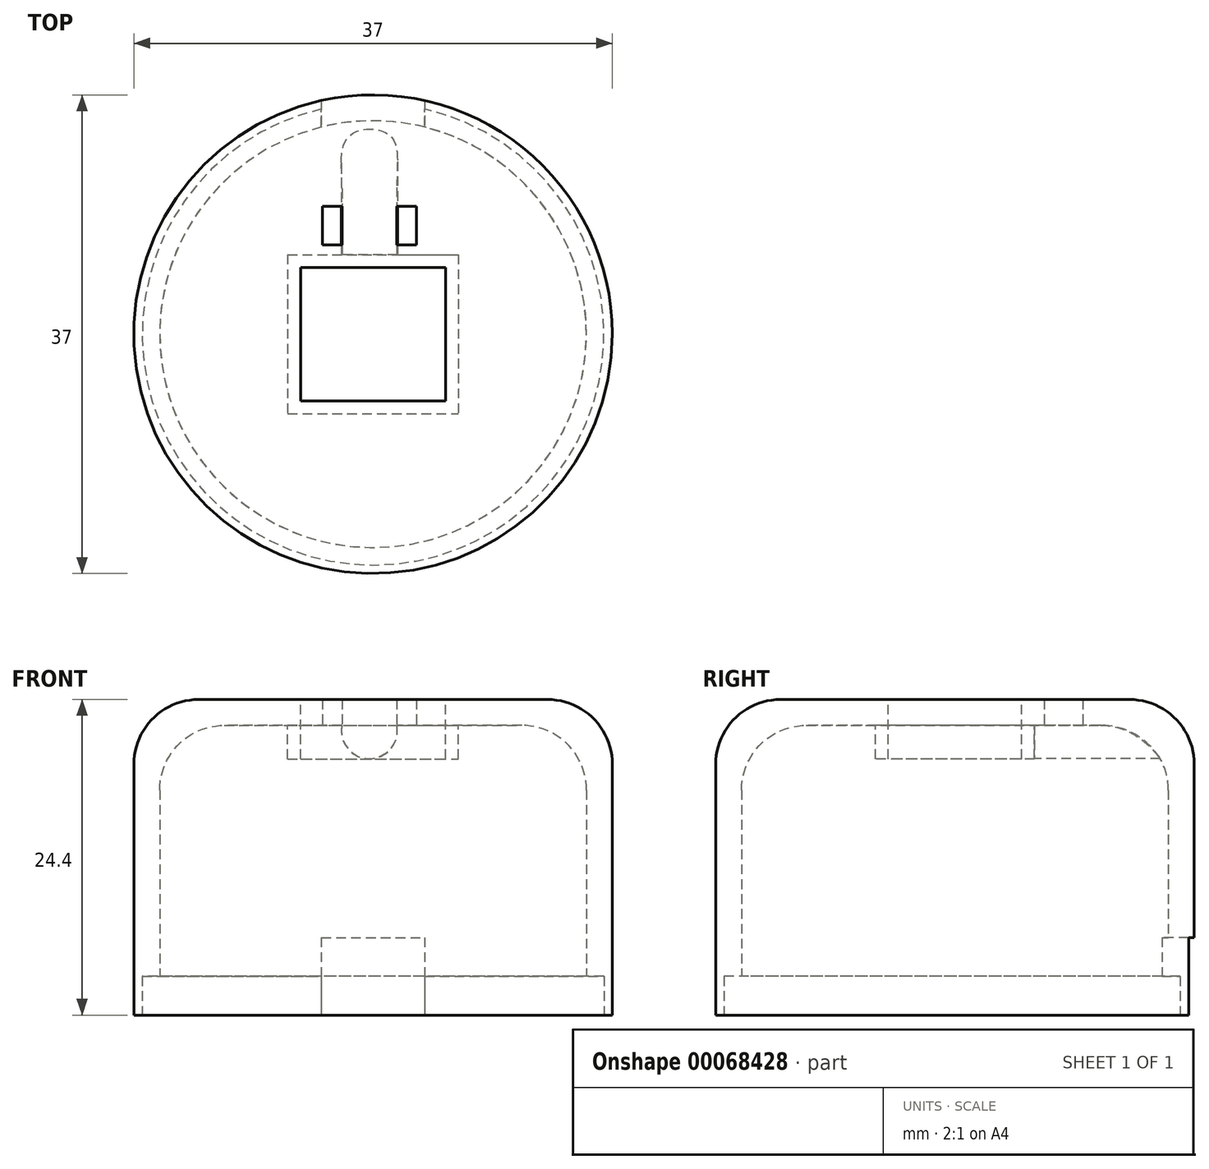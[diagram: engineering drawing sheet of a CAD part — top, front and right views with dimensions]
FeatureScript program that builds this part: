
annotation { "Feature Type Name" : "Feature", "Feature Type Description" : "" }
export const myFeature = defineFeature(function(context is Context, id is Id, definition is map)
    precondition{}
    {
        {
            var Q0;
            Q0=qCreatedBy(makeId("Top.planeOp"),FACE);
            var sketch = newSketch(context, id + "F0", { "sketchPlane" : qUnion([Q0])});
            skCircle(sketch, "E0", {"center": v(0, 0) * mm, "radius": 18.5 * mm});
            skSolve(sketch);
        }
        {
            var Q0;
            Q0=qSketchRegion(id+"F0",true);
            extrude(context, id + "F1", {"entities" : qUnion([Q0]), "depth" : 24.4 * mm});
        }
        {
            var Q0;
            Q0=makeQuery(id+"F1.opExtrude","CAP_FACE",FACE,{"disambiguationData":[OSD([sQuery(id+"F0.wireOp",EDGE,"E0")])],"isStart":true});
            var Q1;
            Q1=makeQuery(id+"F1.opExtrude","SWEPT_BODY",BODY,{"disambiguationData":[OSD([sQuery(id+"F0.wireOp",EDGE,"E0")])]});
            shell(context, id + "F2", {"entities" : qUnion([Q0]), "parts" : qUnion([Q1]), "thickness" : 2 * mm});
        }
        {
            var Q0;
            {var subQ0=sQuery(id+"F0.wireOp",EDGE,"E0");Q0=makeQuery(id+"F2.opShell","OFFSET_EDGE",EDGE,{"disambiguationData":[OSD([subQ0]),TDD([makeQuery(id+"F1.opExtrude","CAP_EDGE",EDGE,{"disambiguationData":[OSD([subQ0])],"isStart":false})])]});}
            fillet(context, id + "F3", {"entities" : qUnion([Q0]), "radius" : 5 * mm, "tangentPropagation" : true, "allowEdgeOverflow" : false});
        }
        {
            var Q0;
            Q0=makeQuery(id+"F1.opExtrude","CAP_EDGE",EDGE,{"disambiguationData":[OSD([sQuery(id+"F0.wireOp",EDGE,"E0")])],"isStart":false});
            fillet(context, id + "F4", {"entities" : qUnion([Q0]), "radius" : 5 * mm, "tangentPropagation" : true, "allowEdgeOverflow" : false});
        }
        {
            var Q0;
            Q0=makeQuery(id+"F1.opExtrude","CAP_FACE",FACE,{"disambiguationData":[OSD([sQuery(id+"F0.wireOp",EDGE,"E0")])],"isStart":false});
            var sketch = newSketch(context, id + "F5", { "sketchPlane" : qUnion([Q0])});
            skLineSegment(sketch, "E1.rect.bottom", {"start": v(-5.6, 5.15) * mm, "end": v(5.6, 5.15) * mm});
            skLineSegment(sketch, "E1.rect.top", {"start": v(-5.6, -5.15) * mm, "end": v(5.6, -5.15) * mm});
            skLineSegment(sketch, "E1.rect.left", {"start": v(-5.6, 5.15) * mm, "end": v(-5.6, -5.15) * mm});
            skLineSegment(sketch, "E1.rect.right", {"start": v(5.6, 5.15) * mm, "end": v(5.6, -5.15) * mm});
            skPoint(sketch, "E1.rect.middle", {"position": v(0, 0) * mm});
            skLineSegment(sketch, "E2.0", {"start": v(-6.6, 6.15) * mm, "end": v(-6.6, -6.15) * mm});
            skLineSegment(sketch, "E2.1", {"start": v(-6.6, 6.15) * mm, "end": v(6.6, 6.15) * mm});
            skLineSegment(sketch, "E2.2", {"start": v(6.6, 6.15) * mm, "end": v(6.6, -6.15) * mm});
            skLineSegment(sketch, "E2.3", {"start": v(-6.6, -6.15) * mm, "end": v(6.6, -6.15) * mm});
            skSolve(sketch);
        }
        {
            var Q0;
            Q0=makeQuery(id+"F5.imprint","IMPRINT",FACE,{"disambiguationData":[TD([[makeQuery(id+"F5.imprint","IMPRINT",EDGE,{"derivedFrom":sQuery(id+"F5.wireOp",EDGE,"E1.rect.bottom")}),-1.0]])]});
            extrude(context, id + "F6", {"entities" : qUnion([Q0]), "operationType" : NewBodyOperationType.REMOVE, "oppositeDirection" : true, "depth" : 25 * mm});
        }
        {
            var Q0;
            Q0=makeQuery(id+"F1.opExtrude","CAP_FACE",FACE,{"disambiguationData":[OSD([sQuery(id+"F0.wireOp",EDGE,"E0")])],"isStart":true});
            var sketch = newSketch(context, id + "F7", { "sketchPlane" : qUnion([Q0])});
            skLineSegment(sketch, "E3.rect.bottom", {"start": v(4, -20.4) * mm, "end": v(-4, -20.4) * mm});
            skLineSegment(sketch, "E3.rect.top", {"start": v(4, 12.5) * mm, "end": v(-4, 12.5) * mm});
            skLineSegment(sketch, "E3.rect.left", {"start": v(4, -20.4) * mm, "end": v(4, 12.5) * mm});
            skLineSegment(sketch, "E3.rect.right", {"start": v(-4, -20.4) * mm, "end": v(-4, 12.5) * mm});
            skPoint(sketch, "E3.rect.middle", {"position": v(0, 0) * mm});
            skSolve(sketch);
        }
        {
            var Q0;
            Q0=qSketchRegion(id+"F7",true);
            extrude(context, id + "F8", {"entities" : qUnion([Q0]), "operationType" : NewBodyOperationType.REMOVE, "oppositeDirection" : true, "depth" : 6 * mm});
        }
        {
            var Q0;
            {var subQ0=sQuery(id+"F0.wireOp",EDGE,"E0");Q0=makeQuery(id+"F8.boolean.opBoolean","SPLIT",FACE,{"disambiguationData":[TD([makeQuery(id+"F8.opExtrude","SWEPT_FACE",FACE,{"disambiguationData":[OSD([sQuery(id+"F7.wireOp",EDGE,"E3.rect.right")])]})])],"derivedFrom":makeQuery(id+"F1.opExtrude","CAP_FACE",FACE,{"disambiguationData":[OSD([subQ0])],"isStart":true})});}
            var sketch = newSketch(context, id + "F9", { "sketchPlane" : qUnion([Q0])});
            skCircle(sketch, "E4", {"center": v(0, 0) * mm, "radius": 17.85 * mm});
            skSolve(sketch);
        }
        {
            var Q0;
            Q0 = qSketchRegion(id + "F9", true);
            var Q1;
            Q1 = qSketchRegion(id + "F7", true);
            extrude(context, id + "F10", {"entities" : qUnion([Q0, Q1]), "operationType" : NewBodyOperationType.REMOVE, "oppositeDirection" : true, "depth" : 3 * mm});
        }
        {
            var Q0;
            Q0=makeQuery(id+"F5.imprint","IMPRINT",FACE,{"disambiguationData":[TD([[makeQuery(id+"F5.imprint","IMPRINT",EDGE,{"derivedFrom":sQuery(id+"F5.wireOp",EDGE,"E1.rect.bottom")}),1.0]])]});
            extrude(context, id + "F11", {"entities" : qUnion([Q0]), "operationType" : NewBodyOperationType.ADD, "oppositeDirection" : true, "depth" : 4.6 * mm});
        }
        {
            var Q0;
            Q0=makeQuery(id+"F11.opExtrude","SWEPT_FACE",FACE,{"disambiguationData":[OSD([sQuery(id+"F5.wireOp",EDGE,"E2.1")])]});
            var sketch = newSketch(context, id + "F12", { "sketchPlane" : qUnion([Q0])});
            skArc(sketch, "E5", {"start": v(-1.84, 22.4) * mm, "mid": v(0.28, 19.82) * mm, "end": v(2.4, 22.4) * mm});
            skSolve(sketch);
        }
        {
            var Q0;
            {var subQ0=sQuery(id+"F12.wireOp",EDGE,"E5");Q0=makeQuery(id+"F12.imprint","IMPRINT",FACE,{"disambiguationData":[TD([[makeQuery(id+"F12.imprint","IMPRINT",EDGE,{"derivedFrom":subQ0}),1.0]])]});}
            extrude(context, id + "F13", {"entities" : qUnion([Q0]), "operationType" : NewBodyOperationType.ADD, "depth" : 10 * mm});
        }
        {
            var Q0;
            {var subQ0=sQuery(id+"F0.wireOp",EDGE,"E0");Q0=makeQuery(id+"F2.opShell","OFFSET_FACE",FACE,{"disambiguationData":[OSD([subQ0]),TDD([makeQuery(id+"F1.opExtrude","CAP_FACE",FACE,{"disambiguationData":[OSD([subQ0])],"isStart":false})])]});}
            var sketch = newSketch(context, id + "F14", { "sketchPlane" : qUnion([Q0])});
            skLineSegment(sketch, "E6.bottom", {"start": v(-2.4, -9.89) * mm, "end": v(-3.9, -9.89) * mm});
            skLineSegment(sketch, "E6.top", {"start": v(-2.4, -6.89) * mm, "end": v(-3.9, -6.89) * mm});
            skLineSegment(sketch, "E6.left", {"start": v(-2.4, -9.89) * mm, "end": v(-2.4, -6.89) * mm});
            skLineSegment(sketch, "E6.right", {"start": v(-3.9, -9.89) * mm, "end": v(-3.9, -6.89) * mm});
            skLineSegment(sketch, "E7.bottom", {"start": v(1.84, -6.89) * mm, "end": v(3.34, -6.89) * mm});
            skLineSegment(sketch, "E7.top", {"start": v(1.84, -9.89) * mm, "end": v(3.34, -9.89) * mm});
            skLineSegment(sketch, "E7.left", {"start": v(1.84, -6.89) * mm, "end": v(1.84, -9.89) * mm});
            skLineSegment(sketch, "E7.right", {"start": v(3.34, -6.89) * mm, "end": v(3.34, -9.89) * mm});
            skSolve(sketch);
        }
        {
            var Q0;
            Q0 = qSketchRegion(id + "F14", true);
            extrude(context, id + "F15", {"entities" : qUnion([Q0]), "operationType" : NewBodyOperationType.REMOVE, "oppositeDirection" : true, "depth" : 25 * mm});
        }
    });
